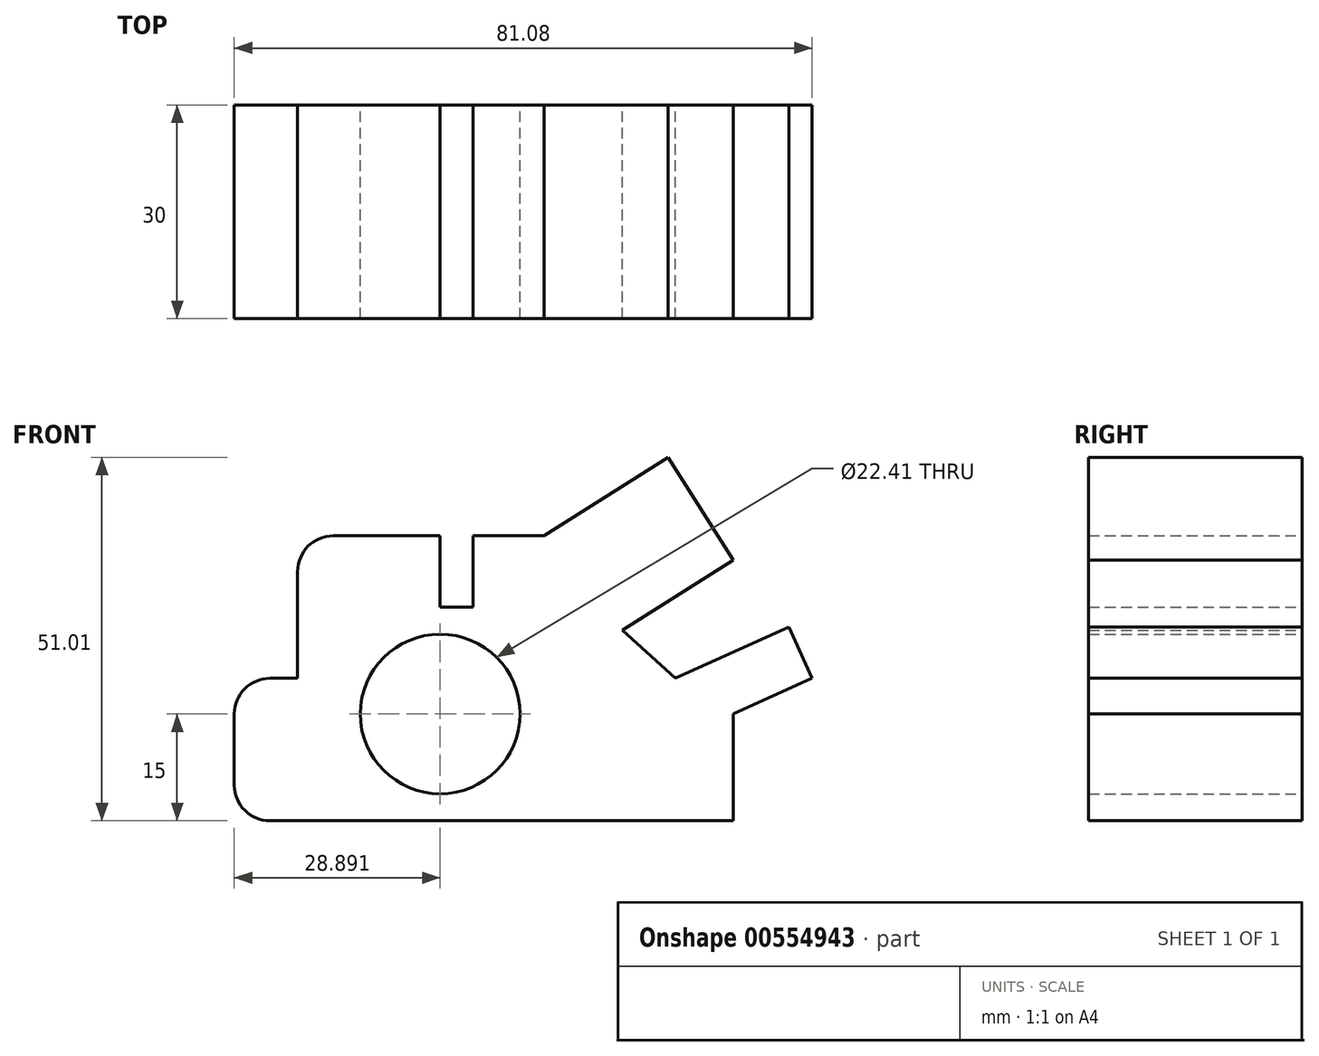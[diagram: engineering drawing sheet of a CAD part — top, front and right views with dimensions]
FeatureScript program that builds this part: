
annotation { "Feature Type Name" : "Feature", "Feature Type Description" : "" }
export const myFeature = defineFeature(function(context is Context, id is Id, definition is map)
    precondition{}
    {
        {
            var Q0;
            Q0=qCreatedBy(makeId("Front.planeOp"),FACE);
            var sketch = newSketch(context, id + "F0", { "sketchPlane" : qUnion([Q0])});
            skLineSegment(sketch, "E0", {"start": v(18.37, -15) * mm, "end": v(18.37, 0) * mm});
            skLineSegment(sketch, "E1", {"start": v(18.37, 0) * mm, "end": v(29.45, 5) * mm});
            skLineSegment(sketch, "E2", {"start": v(29.45, 5) * mm, "end": v(26.2, 12.2) * mm});
            skLineSegment(sketch, "E3", {"start": v(26.2, 12.2) * mm, "end": v(10.23, 5) * mm});
            skLineSegment(sketch, "E4", {"start": v(10.23, 5) * mm, "end": v(2.84, 11.74) * mm});
            skLineSegment(sketch, "E5", {"start": v(2.84, 11.74) * mm, "end": v(18.37, 21.59) * mm});
            skLineSegment(sketch, "E6", {"start": v(18.37, 21.59) * mm, "end": v(9.23, 36.01) * mm});
            skLineSegment(sketch, "E7", {"start": v(9.23, 36.01) * mm, "end": v(-8.15, 25) * mm});
            skLineSegment(sketch, "E8", {"start": v(-8.15, 25) * mm, "end": v(-18.15, 25) * mm});
            skLineSegment(sketch, "E9", {"start": v(-18.15, 25) * mm, "end": v(-18.15, 15) * mm});
            skLineSegment(sketch, "E10", {"start": v(-22.74, 15) * mm, "end": v(-22.74, 25) * mm});
            skLineSegment(sketch, "E11", {"start": v(-22.74, 25) * mm, "end": v(-37.74, 25) * mm});
            skLineSegment(sketch, "E12", {"start": v(-42.74, 20) * mm, "end": v(-42.74, 5) * mm});
            skLineSegment(sketch, "E13", {"start": v(-42.74, 5) * mm, "end": v(-46.63, 5) * mm});
            skLineSegment(sketch, "E14", {"start": v(-51.63, 0) * mm, "end": v(-51.63, -10) * mm});
            skLineSegment(sketch, "E15", {"start": v(-46.63, -15) * mm, "end": v(18.37, -15) * mm});
            skPoint(sketch, "E16.start.orphan", {"position": v(-20.44, 15) * mm});
            skLineSegment(sketch, "E17", {"start": v(-22.74, 15) * mm, "end": v(-18.15, 15) * mm});
            skPoint(sketch, "E18.visualSharp", {"position": v(-51.63, 5) * mm});
            skArc(sketch, "E18.filletArc", {"start": v(-46.63, 5) * mm, "mid": v(-50.16, 3.54) * mm, "end": v(-51.63, 0) * mm});
            skPoint(sketch, "E19.visualSharp", {"position": v(-51.63, -15) * mm});
            skArc(sketch, "E19.filletArc", {"start": v(-51.63, -10) * mm, "mid": v(-50.16, -13.54) * mm, "end": v(-46.63, -15) * mm});
            skPoint(sketch, "E20.visualSharp", {"position": v(-42.74, 25) * mm});
            skArc(sketch, "E20.filletArc", {"start": v(-37.74, 25) * mm, "mid": v(-41.27, 23.54) * mm, "end": v(-42.74, 20) * mm});
            skCircle(sketch, "E21", {"center": v(-22.74, 0) * mm, "radius": 11.2 * mm});
            skSolve(sketch);
        }
        {
            var Q0;
            Q0 = qSketchRegion(id + "F0", true);
            extrude(context, id + "F1", {"entities" : qUnion([Q0]), "depth" : 30 * mm, "offsetDistance" : 25 * mm});
        }
    });
